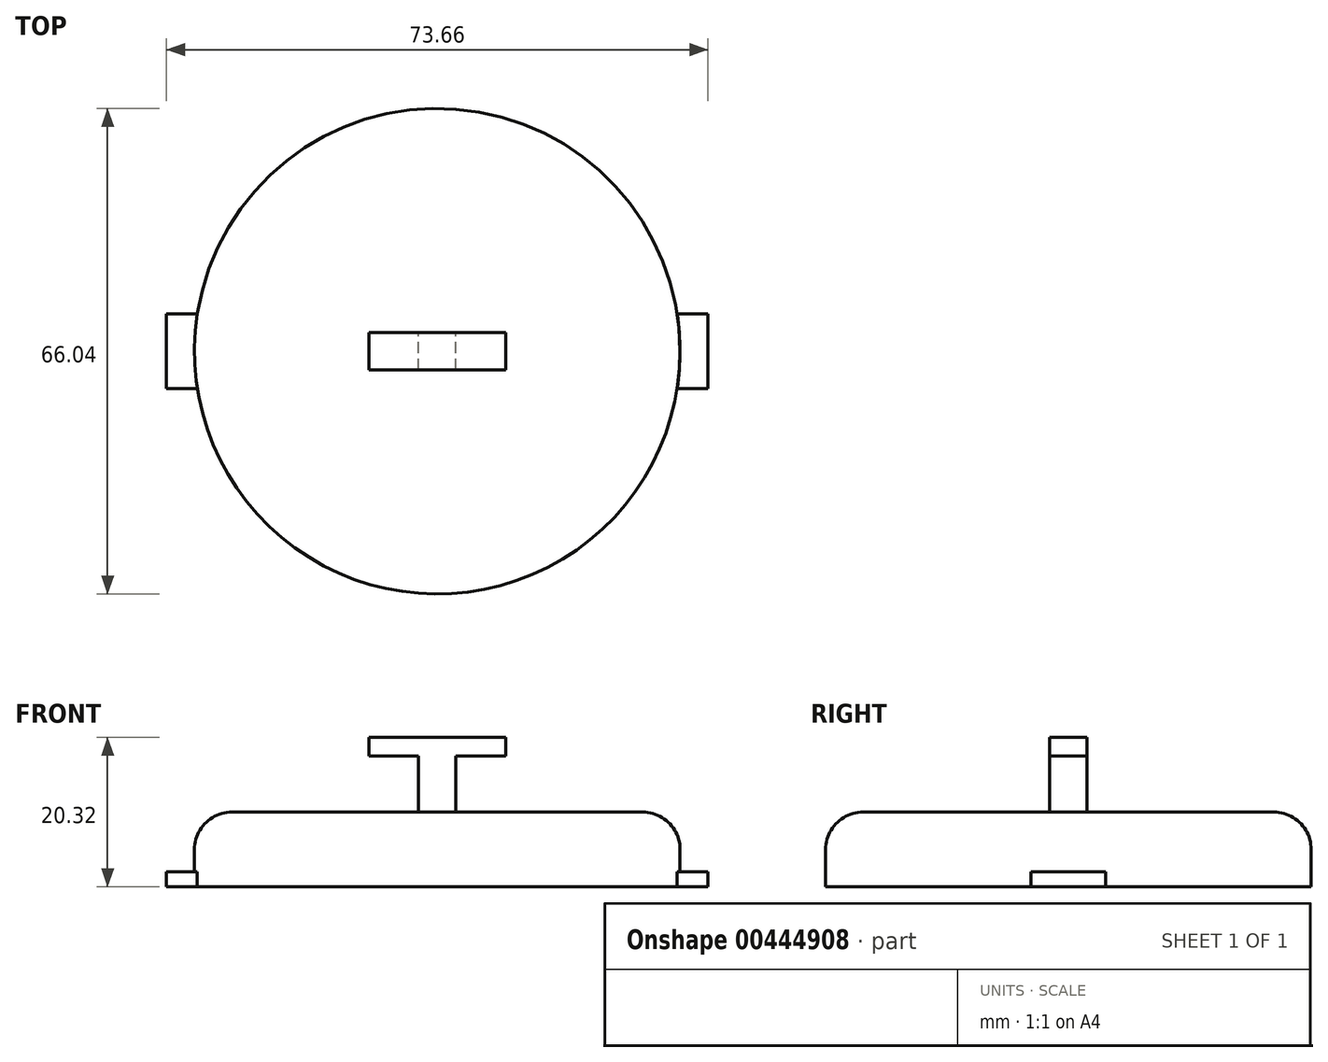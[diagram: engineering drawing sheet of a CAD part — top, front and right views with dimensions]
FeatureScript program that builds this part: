
annotation { "Feature Type Name" : "Feature", "Feature Type Description" : "" }
export const myFeature = defineFeature(function(context is Context, id is Id, definition is map)
    precondition{}
    {
        {
            var Q0;
            Q0=qCreatedBy(makeId("Top.planeOp"),FACE);
            var sketch = newSketch(context, id + "F0", { "sketchPlane" : qUnion([Q0])});
            skCircle(sketch, "E0", {"center": v(0, 0) * mm, "radius": 33.02 * mm});
            skSolve(sketch);
        }
        {
            var Q0;
            Q0=makeQuery(id+"F0.imprint","IMPRINT",FACE,{"disambiguationData":[TD([[makeQuery(id+"F0.imprint","IMPRINT",EDGE,{"derivedFrom":sQuery(id+"F0.wireOp",EDGE,"E0")}),1.0]])]});
            extrude(context, id + "F1", {"entities" : qUnion([Q0]), "depth" : 10.16 * mm});
        }
        {
            var Q0;
            Q0=makeQuery(id+"F1.opExtrude","CAP_FACE",FACE,{"disambiguationData":[OSD([sQuery(id+"F0.wireOp",EDGE,"E0")])],"isStart":false});
            fillet(context, id + "F2", {"entities" : qUnion([Q0]), "radius" : 5.08 * mm, "tangentPropagation" : true, "allowEdgeOverflow" : false});
        }
        {
            var Q0;
            Q0=makeQuery(id+"F1.opExtrude","CAP_FACE",FACE,{"disambiguationData":[OSD([sQuery(id+"F0.wireOp",EDGE,"E0")])],"isStart":false});
            var sketch = newSketch(context, id + "F3", { "sketchPlane" : qUnion([Q0])});
            skLineSegment(sketch, "E1.bottom", {"start": v(-2.54, -2.54) * mm, "end": v(2.54, -2.54) * mm});
            skLineSegment(sketch, "E1.top", {"start": v(-2.54, 2.54) * mm, "end": v(2.54, 2.54) * mm});
            skLineSegment(sketch, "E1.left", {"start": v(-2.54, -2.54) * mm, "end": v(-2.54, 2.54) * mm});
            skLineSegment(sketch, "E1.right", {"start": v(2.54, -2.54) * mm, "end": v(2.54, 2.54) * mm});
            skPoint(sketch, "E1.middle", {"position": v(0, 0) * mm});
            skSolve(sketch);
        }
        {
            var Q0;
            Q0 = qSketchRegion(id + "F3", true);
            extrude(context, id + "F4", {"entities" : qUnion([Q0]), "operationType" : NewBodyOperationType.ADD, "depth" : 7.62 * mm});
        }
        {
            var Q0;
            Q0=makeQuery(id+"F4.opExtrude","CAP_FACE",FACE,{"disambiguationData":[OSD([sQuery(id+"F3.wireOp",EDGE,"E1.bottom"),sQuery(id+"F3.wireOp",EDGE,"E1.top"),sQuery(id+"F3.wireOp",EDGE,"E1.left"),sQuery(id+"F3.wireOp",EDGE,"E1.right")])],"isStart":false});
            var sketch = newSketch(context, id + "F5", { "sketchPlane" : qUnion([Q0])});
            skLineSegment(sketch, "E2.bottom", {"start": v(-9.29, -2.54) * mm, "end": v(9.29, -2.54) * mm});
            skLineSegment(sketch, "E2.top", {"start": v(-9.29, 2.54) * mm, "end": v(9.29, 2.54) * mm});
            skLineSegment(sketch, "E2.left", {"start": v(-9.29, -2.54) * mm, "end": v(-9.29, 2.54) * mm});
            skLineSegment(sketch, "E2.right", {"start": v(9.29, -2.54) * mm, "end": v(9.29, 2.54) * mm});
            skPoint(sketch, "E2.middle", {"position": v(0, 0) * mm});
            skSolve(sketch);
        }
        {
            var Q0;
            Q0 = qSketchRegion(id + "F5", true);
            extrude(context, id + "F6", {"entities" : qUnion([Q0]), "operationType" : NewBodyOperationType.ADD, "depth" : 2.54 * mm});
        }
        {
            var Q0;
            Q0=qCreatedBy(makeId("Top.planeOp"),FACE);
            var sketch = newSketch(context, id + "F7", { "sketchPlane" : qUnion([Q0])});
            skLineSegment(sketch, "E3.bottom", {"start": v(-36.83, 5.08) * mm, "end": v(36.83, 5.08) * mm});
            skLineSegment(sketch, "E3.top", {"start": v(-36.83, -5.08) * mm, "end": v(36.83, -5.08) * mm});
            skLineSegment(sketch, "E3.left", {"start": v(-36.83, 5.08) * mm, "end": v(-36.83, -5.08) * mm});
            skLineSegment(sketch, "E3.right", {"start": v(36.83, 5.08) * mm, "end": v(36.83, -5.08) * mm});
            skPoint(sketch, "E3.middle", {"position": v(0, 0) * mm});
            skSolve(sketch);
        }
        {
            var Q0;
            Q0 = qSketchRegion(id + "F7", true);
            extrude(context, id + "F8", {"entities" : qUnion([Q0]), "operationType" : NewBodyOperationType.ADD, "depth" : 2.03 * mm});
        }
    });
